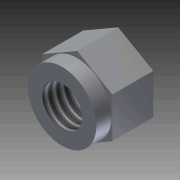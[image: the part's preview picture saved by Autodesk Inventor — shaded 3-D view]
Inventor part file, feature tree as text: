
AUTODESK INVENTOR PART (.ipt)
format: ipt  version: 2011 (Build 150239000, 239)  size: 91,648 bytes
history: native  units: in
note: dims shown in document units (in); Inventor stores cm internally (conversion verified against a paired STEP export)
features: extrude x3, sketch x3, thread x1
ambient origin geometry x8: Origin, YZ Plane, XZ Plane, XY Plane, X Axis, Y Axis, Z Axis, Center Point
bodies: Solid1 (feature_tree)
feature tree (7):
  extrude  "Extrusion1"  Depth=0.325in TaperAngle=0.0deg
  extrude  "Extrusion2"  Depth=0.12in TaperAngle=0.0deg
  extrude  "Extrusion3"  Depth=0.12in TaperAngle=0.0deg
  thread  "Thread1"  [1 undecoded]
  sketch  "Sketch1"  dims[d0=0.555in d1=0.325in d2=0.0in]
  sketch  "Sketch2"  dims[d3=0.543in d4=0.12in d5=0.0in]
  sketch  "Sketch3"  dims[d6=0.315in d7=0.12in d8=0.0in d9=1.0in d10=0.0in]
note: 1 required parameter value undecoded (feature->parameter linkage not recoverable at this tier; creation-order binding heuristic only, values carry confidence <= 0.55)
